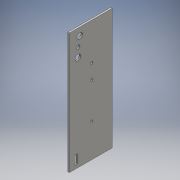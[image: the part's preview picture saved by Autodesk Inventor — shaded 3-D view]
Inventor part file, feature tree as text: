
AUTODESK INVENTOR PART (.ipt)
format: ipt  version: 2016 (Build 200138000, 138)  size: 120,832 bytes
history: native  units: mm
features: extrude x1, sketch x1
ambient origin geometry x8: Origin, YZ Plane, XZ Plane, XY Plane, X Axis, Y Axis, Z Axis, Center Point
bodies: Solid1 (feature_tree)
feature tree (2):
  extrude  "Extrusion1"  Depth=128.0mm
  sketch  "Sketch1"  dims[d0=45.3mm d1=128.0mm d2=6.0mm d3=4.0mm d4=6.0mm d5=8.0mm d6=17.5mm d7=27.0mm d8=11.0mm d9=9.0mm d10=9.0mm d11=2.5mm d12=39.25mm d13=23.5mm d14=2.5mm d15=54.75mm d16=23.5mm d17=2.5mm d18=23.5mm d19=92.75mm d20=3.0mm d21=9.0mm d22=115.0mm d23=5.5mm d24=1.6mm d25=0.0mm]
